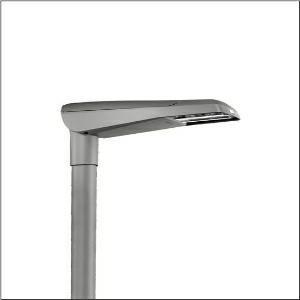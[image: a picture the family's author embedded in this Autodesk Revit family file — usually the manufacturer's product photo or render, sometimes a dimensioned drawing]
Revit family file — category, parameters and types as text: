
# Revit family: streetlight_sl_11_iq_micro___p1_0a_5xc1c51f08ce_61b4
name_source: partatom
category: Lighting Fixtures
units: mm (PartAtom-declared; Revit-internal decimal feet)

## family parameters
Cut with Voids When Loaded = No
Host = Face
Light Source = No
Part Type = Normal
Room Calculation Point = No
Round Connector Dimension = Use Diameter
Shared = No

## types (1)
- --- (1 x LED, 1600 lm, 10.8 W, 3000K)
    Apparent Load = 11 VA
    CIE Flux Codes = 29 63 93 100 100
    Color Rendering = 70
    Color Temperature = 3000K
    Default Elevation = 1800 mm
    Description = Streetlight SL 11 iQ micro, mast luminaire, primary light control with 3 zone facetted reflector, of plastic, silver coated, highly specular, primary optical cover: cover, of PMMA, transparent, light distribution: P1.0a, light emission: direct distribution, primary light characteristic: asymmetric, installation type: post-top, side-entry, lamps: LED, High Power LED, rated values: 1.600lm | 10,8W | 148,1lm/W (begin service life); end service life: 1.600lm | 11,1W; at 50% lumin. flux: 800lm | 6W | 133,3lm/W, colour temperature: 3000K, colour rendering: CRI > 70, light colour: 730, light setting 1 begin service life: 100% | 1.600lm | 10,8W | 148,1lm/W | 3.000K, light setting 1 end service life: 11,1W, further light settings possible, control: Street-Remote, optimised constant luminous flux control (CLO 2.0), Desk-Remote (wireless, voltage-free reading and setting of iQ features in the workshop via application-optimized NFC function/RFID function), Light-Fading, Smart-Wire, Night-Set, Lumen-Switch, Temp-Guard, Auto-Match, with cable H07RN-F 3x 1.5mm², mains connection: 230..240V, AC, 50/60Hz, connection cable pre-assembled, cable length: 5,5m, luminaire housing, of diecast aluminium, powder-coated, SITECO metallic grey (DB 702S), please order mast flange separately, inclination adjustable without tools: 0°, 5°, 10°, 15° (post-top) | 0°, -5°, -10°, -15° (side-entry), sealing non-destructively replaceable, multi-level sealing system, length: 600mm, width: 174mm, height: 116mm, mast flange for spigot size: 42mm (side-entry): 5XC10008XM4, 60/48mm (side-entry/post-top): 5XC10108XM2, 76/60mm (side-entry/post-top): 5XC10108XM1, equipment: standard, protection rating (complete): IP66, insulation class (complete): insulation class II (safety insulation), certification: CE, ENEC, ENEC+, VDE, impact resistance: IK10, permissible operating ambient temperature for outdoor applications: -25..+50°C, standard-compliant lighting for roads and squares, Environmental Product Declaration (EPD) tested and certified by an independent institute, packaging unit: 1 piece

Light Distribution: P1.0a
    Height = 116 mm
    Lamp = 1 x LED
    Lamp Light Flux = 1600 lm
    Lamp Power = 10.8 W
    Lamp count = 1
    Length = 600 mm
    Luminous efficacy = 148 lm/W
    Manufacturer = Siteco
    ModVariant = No
    Model = 5XC1C51F08CE
    Number of Poles = 1
    OnlyDefault = Yes
    Power Factor = 1
    Product Name = Streetlight SL 11 iQ micro | P1.0a
    Product group = mast luminaire | pylon top
    ProductGroupID = 6100
    Protection Class = Protection class II
    Protection Degree = IP 66
    RLX_Detail_Level = 1
    RLX_Emergency_Light_Flux = 0 lm
    RLX_Emergency_Type = 0
    RLX_Emergency_Type_DB = No
    RlxData = <blob elided: 26649 chars, md5=466c8e9e>
    Socket = socket
    Standby Power = 0 W
    System Light Flux = 1600 lm
    System Power = 11 W
    Type Comments = factory setting: luminous flux: 100 % | dim-lin: 254 | 194 mA
    Type Image = l_1006566.jpg
    URL = http://relux.com
    VarID = @adj_019243
    Voltage = 0 V
    Weight = 0.00 kg
    Width = 174 mm

## geometry (parser evidence)
native form markers: Blend x4, Sweep x11
no freeform markers — native parametric forms only
